annotation { "Feature Type Name" : "Feature", "Feature Type Description" : "" }
export const myFeature = defineFeature(function(context is Context, id is Id, definition is map)
    precondition{}
    {
        {
            var Q0;
            Q0=qCreatedBy(makeId("Front.planeOp"),FACE);
            var sketch = newSketch(context, id + "F0", { "sketchPlane" : qUnion([Q0])});
            skLineSegment(sketch, "E0.bottom", {"start": v(-120.94, -46.44) * mm, "end": v(-19.34, -46.44) * mm});
            skLineSegment(sketch, "E0.top", {"start": v(-120.94, -21.3) * mm, "end": v(-19.34, -21.3) * mm});
            skLineSegment(sketch, "E0.left", {"start": v(-120.94, -46.44) * mm, "end": v(-120.94, -21.3) * mm});
            skLineSegment(sketch, "E0.right", {"start": v(-19.34, -46.44) * mm, "end": v(-19.34, -21.3) * mm});
            skArc(sketch, "E1", {"start": v(-19.34, -46.44) * mm, "mid": v(-6.77, -33.87) * mm, "end": v(-19.34, -21.3) * mm});
            skCircle(sketch, "E2", {"center": v(-18.98, -33.87) * mm, "radius": 7.62 * mm});
            skSolve(sketch);
        }
        {
            var Q0;
            Q0 = qSketchRegion(id + "F0", true);
            extrude(context, id + "F1", {"entities" : qUnion([Q0]), "depth" : 11 * mm, "offsetDistance" : 25.4 * mm});
        }
        {
            var Q0;
            Q0=qCreatedBy(makeId("Front.planeOp"),FACE);
            var sketch = newSketch(context, id + "F2", { "sketchPlane" : qUnion([Q0])});
            skText(sketch, "E3", { "text": "Alex Carroll", "fontName": "OpenSans-Regular.ttf"});
            const initialGuessF2  = {"E3": [-0.1125, -0.03919, 1, 0, 0.01113]};
            skSetInitialGuess(sketch, initialGuessF2);
            skSolve(sketch);
        }
        {
            var Q0;
            Q0 = qSketchRegion(id + "F2", true);
            extrude(context, id + "F3", {"entities" : qUnion([Q0]), "depth" : 13 * mm, "offsetDistance" : 25.4 * mm});
        }
    });